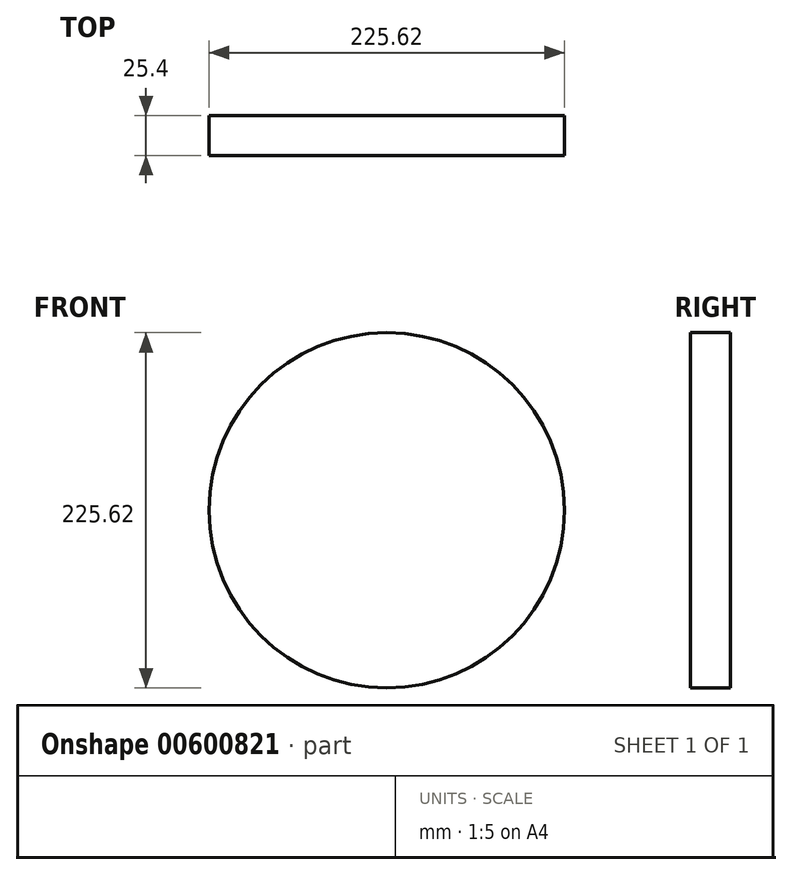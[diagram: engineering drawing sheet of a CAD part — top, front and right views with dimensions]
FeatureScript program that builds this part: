
annotation { "Feature Type Name" : "Feature", "Feature Type Description" : "" }
export const myFeature = defineFeature(function(context is Context, id is Id, definition is map)
    precondition{}
    {
        {
            var Q0;
            Q0=qCreatedBy(makeId("Front.planeOp"),FACE);
            var sketch = newSketch(context, id + "F0", { "sketchPlane" : qUnion([Q0])});
            skCircle(sketch, "E0", {"center": v(0, 0) * mm, "radius": 112.81 * mm});
            skSolve(sketch);
        }
        {
            var Q0;
            Q0 = qSketchRegion(id + "F0", true);
            var Q1;
            Q1=makeQuery(id+"F0.imprint","IMPRINT",FACE,{"disambiguationData":[TD([[makeQuery(id+"F0.imprint","IMPRINT",EDGE,{"derivedFrom":sQuery(id+"F0.wireOp",EDGE,"E0")}),1.0]])]});
            extrude(context, id + "F1", {"entities" : qUnion([Q0, Q1]), "depth" : 25.4 * mm, "offsetDistance" : 25.4 * mm});
        }
        {
            var Q0;
            Q0=makeQuery(id+"F0.imprint","IMPRINT",FACE,{"disambiguationData":[TD([[makeQuery(id+"F0.imprint","IMPRINT",EDGE,{"derivedFrom":sQuery(id+"F0.wireOp",EDGE,"E0")}),1.0]])]});
            extrude(context, id + "F2", {"entities" : qUnion([Q0]), "operationType" : NewBodyOperationType.ADD, "depth" : 25.4 * mm, "offsetDistance" : 25.4 * mm});
        }
    });
